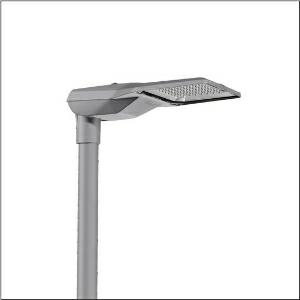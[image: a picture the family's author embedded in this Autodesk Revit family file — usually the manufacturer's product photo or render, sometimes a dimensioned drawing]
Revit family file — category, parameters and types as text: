
# Revit family: streetlight_sl_21_midi___st0_5a_5xe3b33s08nb_b3d9
name_source: partatom
category: Lighting Fixtures
units: mm (PartAtom-declared; Revit-internal decimal feet)

## family parameters
Cut with Voids When Loaded = No
Host = Face
Light Source = No
Part Type = Normal
Room Calculation Point = No
Round Connector Dimension = Use Diameter
Shared = No

## types (1)
- --- (1 x LED, 22700 lm, 151.2 W, 3000K)
    Apparent Load = 151 VA
    CIE Flux Codes = 43 76 97 100 100
    Color Rendering = 70
    Color Temperature = 3000K
    Default Elevation = 1800 mm
    Description = Streetlight SL 21 midi, mast luminaire, primary light control with lens, of PMMA, primary optical cover: cover, of toughened safety glass, transparent, light distribution: ST0.5a, light emission: direct distribution, primary light characteristic: asymmetric, installation type: side-entry, post-top, LED, High Power LED, rated luminous flux: 22.700lm, luminous efficacy: 150lm/W, light colour: 730, colour temperature: 3000K, control gear: D4i, control: overheat protection, constant luminous flux control, time-dependent luminous flux control, flexible luminous flux parameterisation, pre-setting: logarithmic dimming characteristic, mains connection: 230..240V, AC, 50/60Hz, start of lifetime: 151W, end of service life: 157W, reduction: 70W, luminaire housing, of diecast aluminium, powder-coated, SITECO metallic grey (DB 702S), corrosivity category C5 high according to DIN EN ISO 12944, please order mast flange separately, inclination adjustable: 0°, 5°, 10°, 15°, sealing non-destructively replaceable, multi-level sealing system, length: 644mm, width: 335mm, height: 110mm, mast flange for spigot size: 42mm (side-entry): 5XC10008XM4, 60/48mm (side-entry/post-top): 5XC10108XM2, 76/60mm (side-entry/post-top): 5XC10108XM1, mounting height: 4..8m, Smart Interface above, protection rating (complete): IP66, insulation class (complete): insulation class II (safety insulation), certification: CE, ENEC, ENEC+, VDE, impact resistance: IK10, permissible operating ambient temperature for outdoor applications: -40..+50°C, standard-compliant lighting for roads and squares, packaging unit: 1 piece

Light Distribution: ST0.5a
    Height = 111 mm
    Lamp = 1 x LED
    Lamp Light Flux = 22700 lm
    Lamp Power = 151.2 W
    Lamp count = 1
    Length = 644 mm
    Luminous efficacy = 150 lm/W
    Manufacturer = Siteco
    ModVariant = No
    Model = 5XE3B33S08NB
    Number of Poles = 1
    OnlyDefault = Yes
    Power Factor = 1
    Product Name = Streetlight SL 21 midi | ST0.5a
    Product group = mast luminaire | pylon top
    ProductGroupID = 6100
    Protection Class = Protection class II
    Protection Degree = IP 66
    RLX_Detail_Level = 1
    RLX_Emergency_Light_Flux = 0 lm
    RLX_Emergency_Type = 0
    RLX_Emergency_Type_DB = No
    RlxData = <blob elided: 38117 chars, md5=eeaf1f58>
    Socket = socket
    Standby Power = 0 W
    System Light Flux = 22700 lm
    System Power = 151 W
    Type Comments = factory setting: luminous flux: 100 % | dim-lin: 254 | 802 mA
    Type Image = l_1004302.jpg
    URL = http://relux.com
    VarID = @adj_170905
    Voltage = 0 V
    Weight = 0.00 kg
    Width = 336 mm

## geometry (parser evidence)
native form markers: Blend x4, Sweep x8
no freeform markers — native parametric forms only
